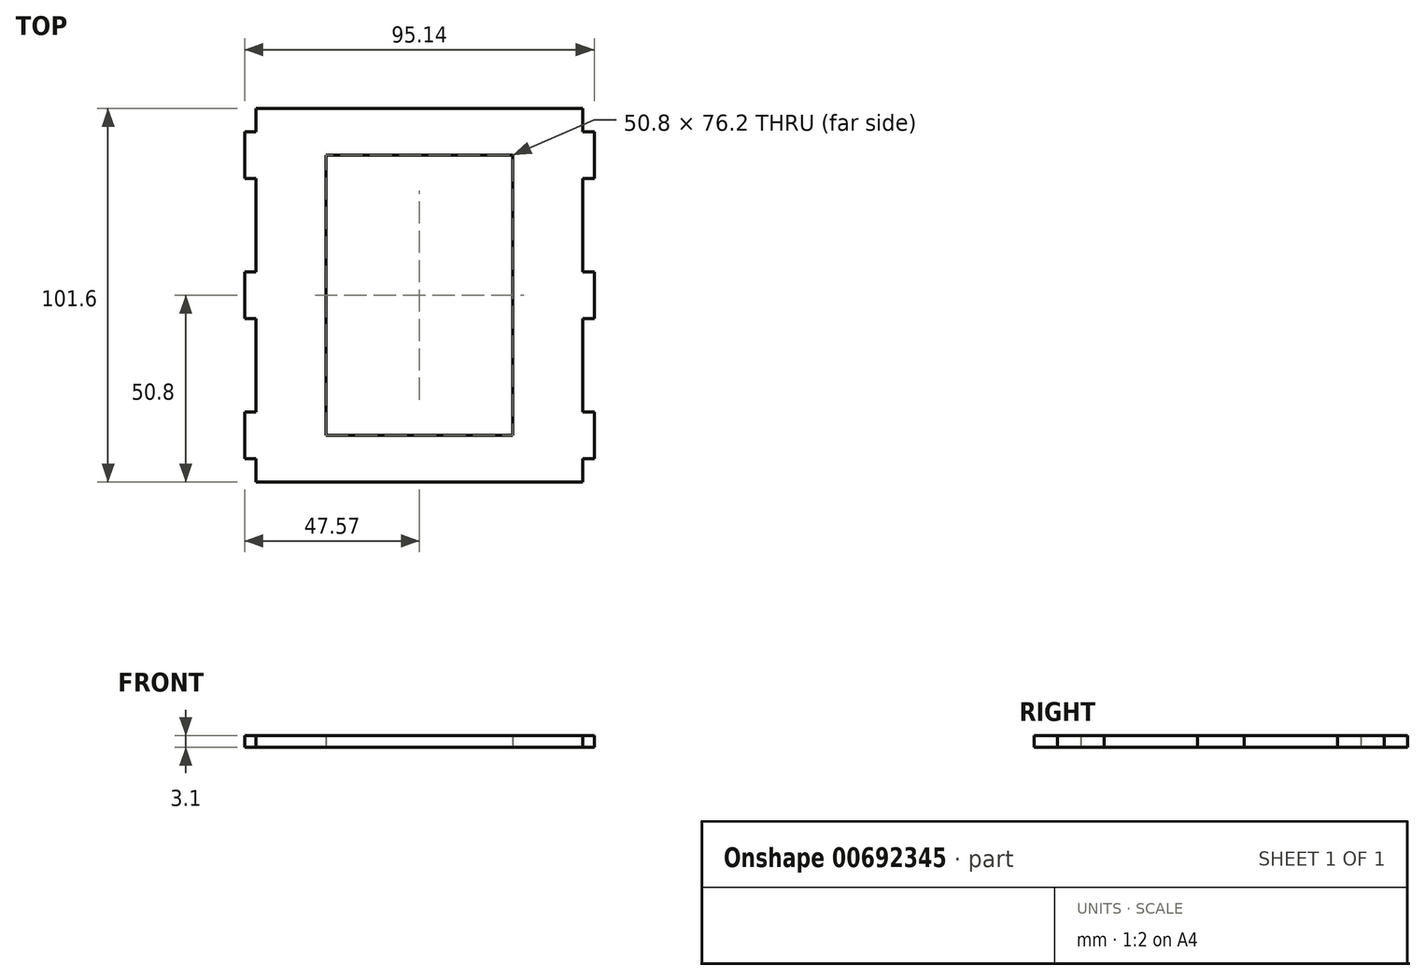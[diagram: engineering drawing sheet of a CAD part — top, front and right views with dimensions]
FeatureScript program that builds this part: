
annotation { "Feature Type Name" : "Feature", "Feature Type Description" : "" }
export const myFeature = defineFeature(function(context is Context, id is Id, definition is map)
    precondition{}
    {
        {
            var Q0;
            Q0=qCreatedBy(makeId("Top.planeOp"),FACE);
            var sketch = newSketch(context, id + "F0", { "sketchPlane" : qUnion([Q0])});
            skLineSegment(sketch, "E0.bottom", {"start": v(-44.45, 50.8) * mm, "end": v(44.45, 50.8) * mm});
            skLineSegment(sketch, "E0.top", {"start": v(-44.45, -50.8) * mm, "end": v(44.45, -50.8) * mm});
            skLineSegment(sketch, "E0.left", {"start": v(-44.45, 50.8) * mm, "end": v(-44.45, 44.45) * mm});
            skLineSegment(sketch, "E0.right", {"start": v(44.45, 50.8) * mm, "end": v(44.45, 44.45) * mm});
            skPoint(sketch, "E0.middle", {"position": v(0, 0) * mm});
            skLineSegment(sketch, "E1.bottom", {"start": v(-44.45, 6.35) * mm, "end": v(-47.57, 6.35) * mm});
            skLineSegment(sketch, "E1.top", {"start": v(-44.45, -6.35) * mm, "end": v(-47.57, -6.35) * mm});
            skLineSegment(sketch, "E1.right", {"start": v(-47.57, 6.35) * mm, "end": v(-47.57, -6.35) * mm});
            skPoint(sketch, "E1.middle", {"position": v(-46.01, 0) * mm});
            skLineSegment(sketch, "E2.bottom", {"start": v(-44.45, 44.45) * mm, "end": v(-47.57, 44.45) * mm});
            skLineSegment(sketch, "E2.top", {"start": v(-44.45, 31.75) * mm, "end": v(-47.57, 31.75) * mm});
            skLineSegment(sketch, "E2.right", {"start": v(-47.57, 44.45) * mm, "end": v(-47.57, 31.75) * mm});
            skPoint(sketch, "E2.middle", {"position": v(-46.01, 38.1) * mm});
            skLineSegment(sketch, "E3.MirrorCS", {"start": v(-44.45, -31.75) * mm, "end": v(-47.57, -31.75) * mm});
            skLineSegment(sketch, "E4.MirrorCS", {"start": v(-44.45, -44.45) * mm, "end": v(-47.57, -44.45) * mm});
            skPoint(sketch, "E5.MirrorP", {"position": v(-46.01, -38.1) * mm});
            skLineSegment(sketch, "E6.MirrorCS", {"start": v(-47.57, -44.45) * mm, "end": v(-47.57, -31.75) * mm});
            skLineSegment(sketch, "E7.trimOffspring", {"start": v(-44.45, 31.75) * mm, "end": v(-44.45, 6.35) * mm});
            skLineSegment(sketch, "E8.trimOffspring", {"start": v(-44.45, -6.35) * mm, "end": v(-44.45, -31.75) * mm});
            skLineSegment(sketch, "E9.trimOffspring", {"start": v(-44.45, -44.45) * mm, "end": v(-44.45, -50.8) * mm});
            skLineSegment(sketch, "E10.bottom", {"start": v(-25.4, 38.1) * mm, "end": v(25.4, 38.1) * mm});
            skLineSegment(sketch, "E10.top", {"start": v(-25.4, -38.1) * mm, "end": v(25.4, -38.1) * mm});
            skLineSegment(sketch, "E10.left", {"start": v(-25.4, 38.1) * mm, "end": v(-25.4, -38.1) * mm});
            skLineSegment(sketch, "E10.right", {"start": v(25.4, 38.1) * mm, "end": v(25.4, -38.1) * mm});
            skLineSegment(sketch, "E11.MirrorCS", {"start": v(44.45, 31.75) * mm, "end": v(47.57, 31.75) * mm});
            skLineSegment(sketch, "E12.MirrorCS", {"start": v(44.45, -44.45) * mm, "end": v(47.57, -44.45) * mm});
            skLineSegment(sketch, "E13.MirrorCS", {"start": v(44.45, 44.45) * mm, "end": v(47.57, 44.45) * mm});
            skLineSegment(sketch, "E14.MirrorCS", {"start": v(44.45, -6.35) * mm, "end": v(47.57, -6.35) * mm});
            skLineSegment(sketch, "E15.MirrorCS", {"start": v(44.45, 6.35) * mm, "end": v(47.57, 6.35) * mm});
            skLineSegment(sketch, "E16.MirrorCS", {"start": v(44.45, -31.75) * mm, "end": v(47.57, -31.75) * mm});
            skPoint(sketch, "E17.MirrorP", {"position": v(46.01, 0) * mm});
            skPoint(sketch, "E18.MirrorP", {"position": v(46.01, -38.1) * mm});
            skLineSegment(sketch, "E19.MirrorCS", {"start": v(47.57, -44.45) * mm, "end": v(47.57, -31.75) * mm});
            skPoint(sketch, "E20.MirrorP", {"position": v(46.01, 38.1) * mm});
            skLineSegment(sketch, "E21.MirrorCS", {"start": v(44.45, 31.75) * mm, "end": v(44.45, 6.35) * mm});
            skLineSegment(sketch, "E22.MirrorCS", {"start": v(47.57, 44.45) * mm, "end": v(47.57, 31.75) * mm});
            skLineSegment(sketch, "E23.MirrorCS", {"start": v(44.45, -6.35) * mm, "end": v(44.45, -31.75) * mm});
            skLineSegment(sketch, "E24.MirrorCS", {"start": v(47.57, 6.35) * mm, "end": v(47.57, -6.35) * mm});
            skLineSegment(sketch, "E25.trimOffspring", {"start": v(44.45, -44.45) * mm, "end": v(44.45, -50.8) * mm});
            skSolve(sketch);
        }
        {
            var Q0;
            Q0 = qSketchRegion(id + "F0", true);
            extrude(context, id + "F1", {"entities" : qUnion([Q0]), "depth" : 3.1 * mm, "offsetDistance" : 25.4 * mm});
        }
    });
